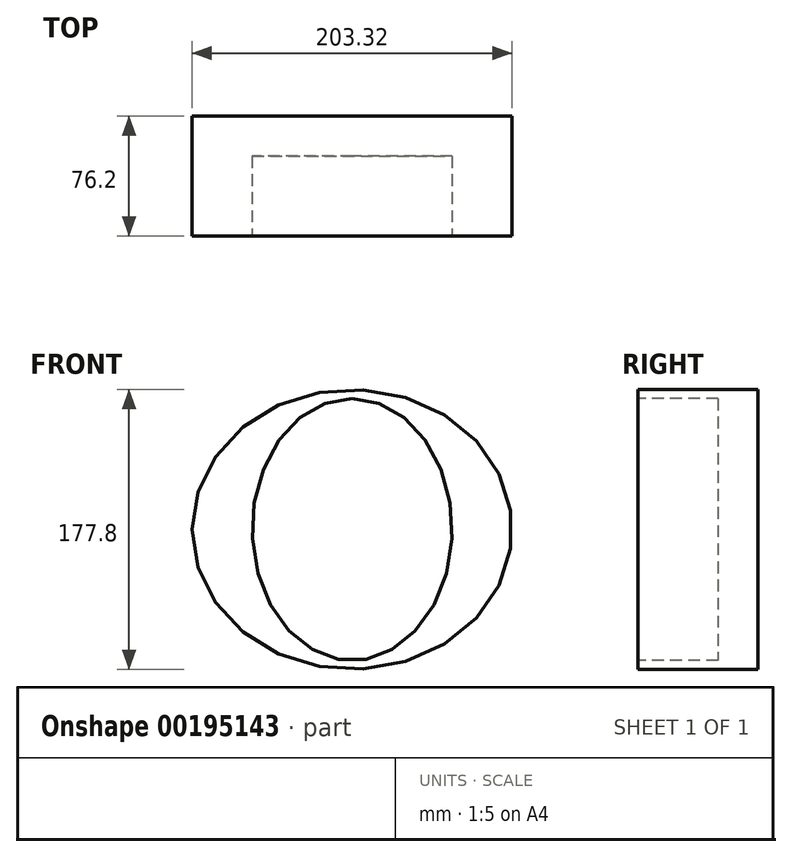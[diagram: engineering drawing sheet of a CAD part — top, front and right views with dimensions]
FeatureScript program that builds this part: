
annotation { "Feature Type Name" : "Feature", "Feature Type Description" : "" }
export const myFeature = defineFeature(function(context is Context, id is Id, definition is map)
    precondition{}
    {
        {
            var Q0;
            Q0=qCreatedBy(makeId("Front.planeOp"),FACE);
            var sketch = newSketch(context, id + "F0", { "sketchPlane" : qUnion([Q0])});
            skEllipse(sketch, "E0", {"center": v(0, 0) * mm, "majorRadius": 88.9 * mm, "minorRadius": 101.66 * mm, "majorAxis": v(0, 1)});
            skSolve(sketch);
        }
        {
            var Q0;
            Q0 = qSketchRegion(id + "F0", true);
            extrude(context, id + "F1", {"entities" : qUnion([Q0]), "depth" : 76.2 * mm});
        }
        {
            var Q0;
            Q0=makeQuery(id+"F1.opExtrude","CAP_FACE",FACE,{"disambiguationData":[OSD([sQuery(id+"F0.wireOp",EDGE,"E0")])],"isStart":false});
            var sketch = newSketch(context, id + "F2", { "sketchPlane" : qUnion([Q0])});
            skEllipse(sketch, "E1", {"center": v(0, 0) * mm, "majorRadius": 83.2 * mm, "minorRadius": 63.5 * mm, "majorAxis": v(0, 1)});
            skSolve(sketch);
        }
        {
            var Q0;
            Q0=makeQuery(id+"F2.imprint","IMPRINT",FACE,{"disambiguationData":[TD([[makeQuery(id+"F2.imprint","IMPRINT",EDGE,{"derivedFrom":sQuery(id+"F2.wireOp",EDGE,"E1")}),1.0]])]});
            extrude(context, id + "F3", {"entities" : qUnion([Q0]), "operationType" : NewBodyOperationType.REMOVE, "oppositeDirection" : true, "depth" : 50.8 * mm});
        }
    });
